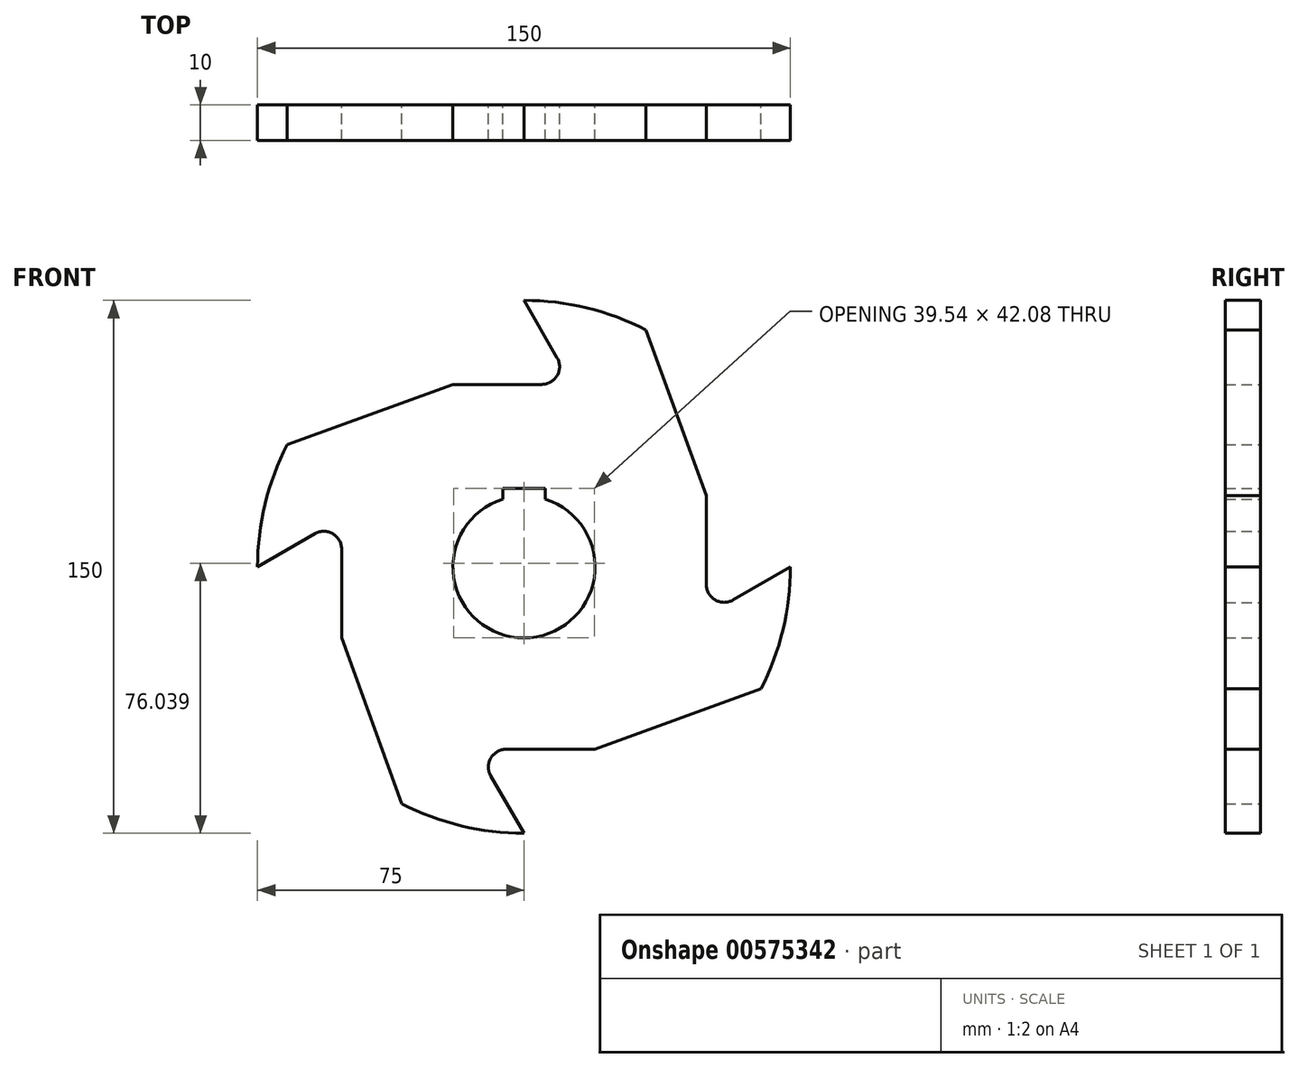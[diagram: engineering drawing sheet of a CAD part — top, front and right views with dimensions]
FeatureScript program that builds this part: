
annotation { "Feature Type Name" : "Feature", "Feature Type Description" : "" }
export const myFeature = defineFeature(function(context is Context, id is Id, definition is map)
    precondition{}
    {
        {
            var Q0;
            Q0=qCreatedBy(makeId("Front.planeOp"),FACE);
            var sketch = newSketch(context, id + "F0", { "sketchPlane" : qUnion([Q0])});
            skArc(sketch, "E0", {"start": v(-66.67, 34.35) * mm, "mid": v(-72.89, 17.67) * mm, "end": v(-75, 0) * mm});
            skLineSegment(sketch, "E1", {"start": v(-75.08, -75) * mm, "end": v(0, -75) * mm});
            skLineSegment(sketch, "E2", {"start": v(0, -75) * mm, "end": v(-9.33, -58.84) * mm});
            skArc(sketch, "E3", {"start": v(-5, -51.34) * mm, "mid": v(-9.33, -53.84) * mm, "end": v(-9.33, -58.84) * mm});
            skLineSegment(sketch, "E4", {"start": v(-5, -51.34) * mm, "end": v(20, -51.34) * mm});
            skLineSegment(sketch, "E5", {"start": v(20, -51.34) * mm, "end": v(66.67, -34.35) * mm});
            skLineSegment(sketch, "E6.1.0", {"start": v(-75, 0) * mm, "end": v(-58.84, 9.33) * mm});
            skArc(sketch, "E6.1.1", {"start": v(-51.34, 5) * mm, "mid": v(-53.84, 9.33) * mm, "end": v(-58.84, 9.33) * mm});
            skLineSegment(sketch, "E6.1.2", {"start": v(-51.34, 5) * mm, "end": v(-51.34, -20) * mm});
            skLineSegment(sketch, "E6.1.3", {"start": v(-51.34, -20) * mm, "end": v(-34.35, -66.67) * mm});
            skLineSegment(sketch, "E6.2.0", {"start": v(0, 75) * mm, "end": v(9.33, 58.84) * mm});
            skArc(sketch, "E6.2.1", {"start": v(5, 51.34) * mm, "mid": v(9.33, 53.84) * mm, "end": v(9.33, 58.84) * mm});
            skLineSegment(sketch, "E6.2.2", {"start": v(5, 51.34) * mm, "end": v(-20, 51.34) * mm});
            skLineSegment(sketch, "E6.2.3", {"start": v(-20, 51.34) * mm, "end": v(-66.67, 34.35) * mm});
            skLineSegment(sketch, "E6.3.0", {"start": v(75, 0) * mm, "end": v(58.84, -9.33) * mm});
            skArc(sketch, "E6.3.1", {"start": v(51.34, -5) * mm, "mid": v(53.84, -9.33) * mm, "end": v(58.84, -9.33) * mm});
            skLineSegment(sketch, "E6.3.2", {"start": v(51.34, -5) * mm, "end": v(51.34, 20) * mm});
            skLineSegment(sketch, "E6.3.3", {"start": v(51.34, 20) * mm, "end": v(34.35, 66.67) * mm});
            skPoint(sketch, "E7.orphan", {"position": v(10.77, 56.34) * mm});
            skPoint(sketch, "E8.orphan", {"position": v(-56.34, 10.77) * mm});
            skPoint(sketch, "E9.orphan", {"position": v(56.34, -10.77) * mm});
            skArc(sketch, "E10.trimOffspring", {"start": v(34.35, 66.67) * mm, "mid": v(17.67, 72.89) * mm, "end": v(0, 75) * mm});
            skArc(sketch, "E11.trimOffspring", {"start": v(66.67, -34.35) * mm, "mid": v(72.89, -17.67) * mm, "end": v(75, 0) * mm});
            skPoint(sketch, "E12.orphan", {"position": v(-10.77, -56.34) * mm});
            skArc(sketch, "E13.trimOffspring", {"start": v(-34.35, -66.67) * mm, "mid": v(-17.67, -72.89) * mm, "end": v(0, -75) * mm});
            skArc(sketch, "E14", {"start": v(-6, 19.08) * mm, "mid": v(0, -20) * mm, "end": v(6, 19.08) * mm});
            skLineSegment(sketch, "E15", {"start": v(-6, 22.08) * mm, "end": v(6, 22.08) * mm});
            skLineSegment(sketch, "E16", {"start": v(-6, 22.08) * mm, "end": v(-6, 19.08) * mm});
            skLineSegment(sketch, "E17", {"start": v(6, 22.08) * mm, "end": v(6, 19.08) * mm});
            skLineSegment(sketch, "E18.trimOffspring", {"start": v(0, 22.08) * mm, "end": v(0, 51.34) * mm});
            skSolve(sketch);
        }
        {
            var Q0;
            Q0 = qSketchRegion(id + "F0", true);
            extrude(context, id + "F1", {"entities" : qUnion([Q0]), "depth" : 10 * mm, "offsetDistance" : 25 * mm});
        }
    });
